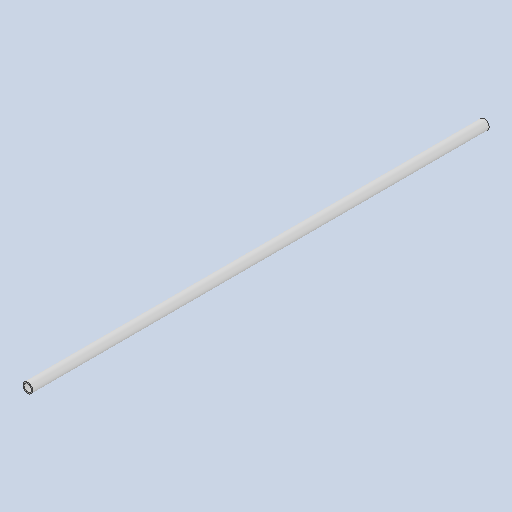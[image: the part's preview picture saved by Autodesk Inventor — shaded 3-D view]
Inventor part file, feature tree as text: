
AUTODESK INVENTOR PART (.ipt)
format: ipt  version: 2025 (Build 290162000, 162)  size: 77,824 bytes
history: native  units: in
note: dims shown in document units (in); Inventor stores cm internally (conversion verified against a paired STEP export)
features: other x3, sketch x1
ambient origin geometry x8: Origin, YZ Plane, XZ Plane, XY Plane, X Axis, Y Axis, Z Axis, Center Point
bodies: Solid1 (feature_tree)
feature tree (4):
  other  "Spar.ipt"
  other  "Solid1::Spar.ipt"
  other  "TaggingFeature1"
  sketch  "Sketch1"  dims[d0=0.3937in]
